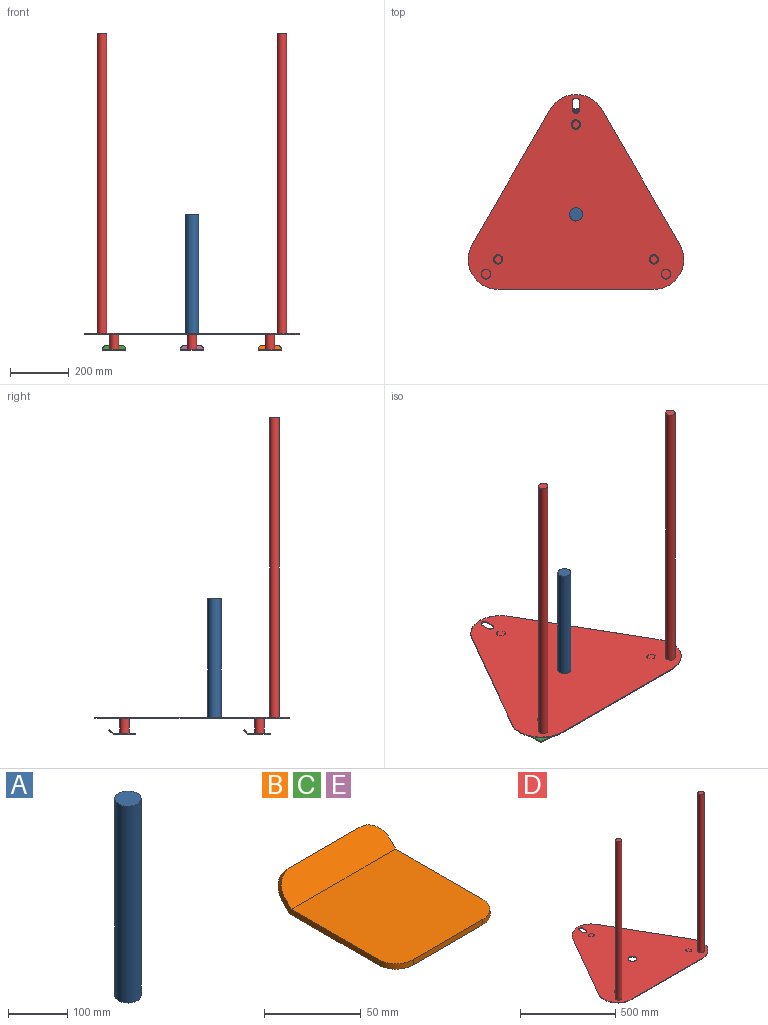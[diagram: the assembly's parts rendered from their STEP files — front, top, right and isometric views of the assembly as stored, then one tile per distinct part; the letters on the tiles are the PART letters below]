
ASSEMBLY  parts=5 mates=4
PART A: 3 faces, bbox 44.5x44.5x406.4 mm
  f0: plane 44.45x44.45mm, normal (0,0,-1), area 1551.8mm2, adj f2
  f1: plane 44.45x44.45mm, normal (0,0,1), area 1551.8mm2, adj f2
  f2: cylinder r=22.23mm len=406.4mm, axis (0,0,1), area 56751.2mm2, adj f0,f1
PART B: 12 faces, bbox 76.2x92.1x16.9 mm
  f0: plane 76.2x13.47mm, normal (0,-0.71,0.71), area 1382.4mm2, adj f1,f5,f6,f7,f9,f11
  f1: plane 76.2x76.2mm, normal (0,0,1), area 5737.2mm2, adj f0,f2,f6,f7,f8,f10
  f2: plane 50.8x3.42mm, normal (0,-1,0), area 173.5mm2, adj f1,f3,f8,f10
  f3: plane 77.62x76.2mm, normal (0,0,-1), area 5845mm2, adj f2,f4,f6,f7,f8,f10
  f4: plane 76.2x14.47mm, normal (0,0.71,-0.71), area 1490.2mm2, adj f3,f5,f6,f7,f9,f11
  f5: plane 50.8x2.42mm, normal (0,0.71,0.71), area 173.5mm2, adj f0,f4,f9,f11
  f6: plane 70.41x7.91mm, normal (1,0,0), area 243.5mm2, adj f0,f1,f3,f4,f10,f11
  f7: plane 70.41x7.91mm, normal (-1,0,0), area 243.5mm2, adj f0,f1,f3,f4,f8,f9
  f8: cylinder r=12.7mm len=12.7mm, axis (0,0,-1), area 68.2mm2, adj f1,f2,f3,f7
  f9: cylinder r=12.7mm len=12.7mm, axis (0,-0.71,0.71), area 68.2mm2, adj f0,f4,f5,f7
  f10: cylinder r=12.7mm len=12.7mm, axis (0,0,1), area 68.2mm2, adj f1,f2,f3,f6
  f11: cylinder r=12.7mm len=12.7mm, axis (0,0.71,-0.71), area 68.2mm2, adj f0,f4,f5,f6
PART C: same geometry as B
PART D: 29 faces, bbox 731.1x660.4x1070.2 mm
  f0: plane 731.13x660.4mm, normal (0,0,-1), area 308947.8mm2, adj f1,f2,f3,f4,f5,f6,f12,f13
  f1: cylinder r=101.6mm len=175.98mm, axis (0,0,1), area 727mm2, adj f0,f2,f6,f7
  f2: plane 457.2x263.96mm, normal (-0.87,0.5,0), area 1803.6mm2, adj f0,f1,f3,f7
  f3: cylinder r=101.6mm len=152.4mm, axis (0,0,1), area 727mm2, adj f0,f2,f4,f7
  f4: plane 527.93x3.42mm, normal (0,-1,0), area 1803.6mm2, adj f0,f3,f5,f7
  f5: cylinder r=101.6mm len=152.4mm, axis (0,0,1), area 727mm2, adj f0,f4,f6,f7
  f6: plane 457.2x263.96mm, normal (0.87,0.5,0), area 1803.6mm2, adj f0,f1,f5,f7
  f7: plane 731.13x660.4mm, normal (0,0,1), area 309739.5mm2, adj f1,f2,f3,f4,f5,f6,f9,f11
  f8: plane 31.75x31.75mm, normal (0,0,1), area 791.7mm2, adj f9
  f9: cylinder r=15.88mm len=1016mm, axis (0,0,1), area 101341.5mm2, adj f7,f8
  f10: plane 31.75x31.75mm, normal (0,0,1), area 791.7mm2, adj f11
  f11: cylinder r=15.88mm len=1016mm, axis (0,0,1), area 101341.5mm2, adj f7,f10
  f12: cylinder r=12.7mm len=25.4mm, axis (0,0,1), area 136.3mm2, adj f0,f7,f13,f14
  f13: plane 25.4x3.42mm, normal (-1,0,0), area 86.8mm2, adj f0,f7,f12,f15
  f14: plane 25.4x3.42mm, normal (1,0,0), area 86.8mm2, adj f0,f7,f12,f15
  f15: cylinder r=12.7mm len=25.4mm, axis (0,0,1), area 136.3mm2, adj f0,f7,f13,f14
  f16: cylinder r=15.88mm len=50.8mm, axis (0,0,-1), area 5067.1mm2, adj f0,f17
  f17: plane 31.75x31.75mm, normal (0,0,-1), area 285mm2, adj f16,f18
  f18: cylinder r=12.7mm len=50.8mm, axis (0,0,-1), area 4053.7mm2, adj f17,f19
  f19: plane 25.4x25.4mm, normal (0,0,-1), area 506.7mm2, adj f18
  f20: cylinder r=12.7mm len=50.8mm, axis (0,0,-1), area 4053.7mm2, adj f21,f23
  f21: plane 31.75x31.75mm, normal (0,0,-1), area 285mm2, adj f20,f22
  f22: cylinder r=15.88mm len=50.8mm, axis (0,0,-1), area 5067.1mm2, adj f0,f21
  f23: plane 25.4x25.4mm, normal (0,0,-1), area 506.7mm2, adj f20
  f24: cylinder r=15.88mm len=50.8mm, axis (0,0,-1), area 5067.1mm2, adj f0,f25
  f25: plane 31.75x31.75mm, normal (0,0,-1), area 285mm2, adj f24,f26
  f26: cylinder r=12.7mm len=50.8mm, axis (0,0,-1), area 4053.7mm2, adj f25,f27
  f27: plane 25.4x25.4mm, normal (0,0,-1), area 506.7mm2, adj f26
  f28: cylinder r=22.23mm len=44.45mm, axis (0,0,1), area 477.1mm2, adj f0,f7
PART E: same geometry as B
PLACE A t=(95.79,425.14,-238.3)mm
PLACE B t=(359.75,-29.31,-234.88)mm
PLACE C t=(-168.18,-29.31,-234.88)mm
PLACE D t=(95.79,425.14,-234.88)mm
PLACE E t=(95.79,427.89,-234.88)mm
MATE fastened D.f20 <-> E.f1  axis (0,0,-1) through (95.79,729.94,-289.1)mm
MATE cylindrical A.f2 <-> D.f28  axis (0,0,1) through (95.79,425.14,-238.3)mm
MATE fastened D.f5 <-> B.f1  axis (0,0,-1) through (359.75,272.74,-289.1)mm
MATE fastened D.f24 <-> C.f1  axis (0,0,-1) through (-168.18,272.74,-289.1)mm
